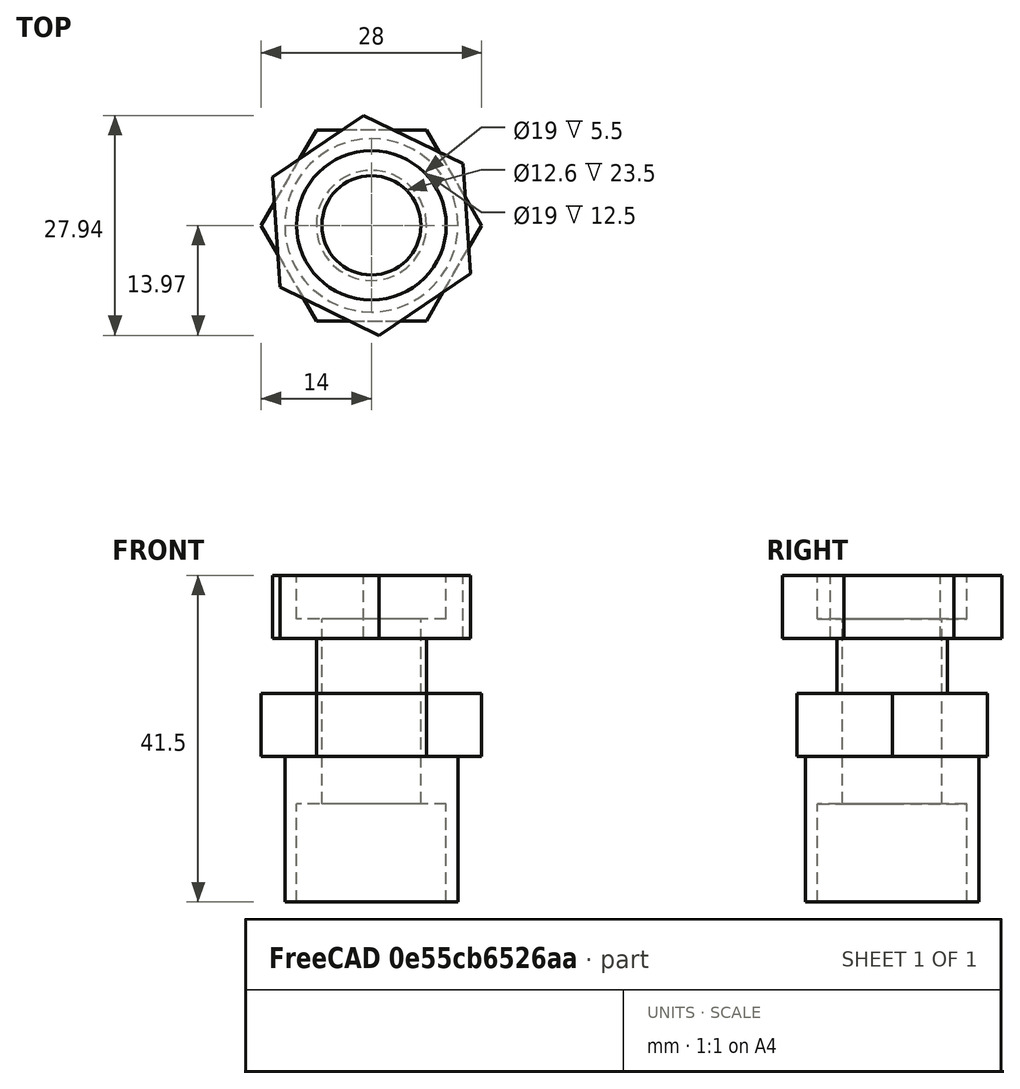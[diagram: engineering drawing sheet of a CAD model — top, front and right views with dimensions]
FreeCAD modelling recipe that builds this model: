
FCSTD DOCUMENT  (FreeCAD 0.16R6706 (Git))
Label: 1_2_ to 3_4_swivel
License: All rights reserved
LicenseURL: http://en.wikipedia.org/wiki/All_rights_reserved
objects: Part::Cylinder×10, Part::Part2DObjectPython×4, Part::FeaturePython×4, Part::Extrusion×4, Part::MultiFuse×4, Part::Cut×2, Part::Fuse×1
note: 29 computed .brp shape members not serialized (recipe doc carries the construction recipe); baked Part::Feature solids carry a one-line shape summary decoded from their .brp

FEATURE [Part::Cylinder] cylinder
  Angle = 360
  Height = 25
  Placement = pos=(0,0,-22.5) rot=(0,0,1;0rad)
  Radius = 11
FEATURE [Part::Cylinder] cylinder001
  Angle = 360
  Height = 30
  Placement = pos=(0,0,-15) rot=(0,0,1;0rad)
  Radius = 7
FEATURE [Part::Part2DObjectPython] polygon  # Draft 2D object (typed FeaturePython)
  ChamferSize = 0
  DrawMode = 0
  FacesNumber = 6
  FilletRadius = 0
  MakeFace = true
  Radius = 14
FEATURE [Part::FeaturePython] RefineLinearExtrude  # WARN: FeaturePython — macro-defined, semantics opaque (R4)
  Base = -> polygon
FEATURE [Part::Extrusion] LinearExtrude
  Base = -> RefineLinearExtrude
  Dir = (0,0,8)
  Placement = pos=(0,0,-4) rot=(0,0,1;0rad)
  Solid = true
FEATURE [Part::Part2DObjectPython] polygon001  # Draft 2D object (typed FeaturePython)
  ChamferSize = 0
  DrawMode = 0
  FacesNumber = 6
  FilletRadius = 0
  MakeFace = true
  Radius = 14
FEATURE [Part::FeaturePython] RefineLinearExtrude001  # WARN: FeaturePython — macro-defined, semantics opaque (R4)
  Base = -> polygon001
FEATURE [Part::Extrusion] LinearExtrude001
  Base = -> RefineLinearExtrude001
  Dir = (0,0,8)
  Placement = pos=(0,0,11) rot=(0,0,1;0.593412rad)
  Solid = true
FEATURE [Part::MultiFuse] Group
  Shapes = -> [cylinder,cylinder001,LinearExtrude,LinearExtrude001]
FEATURE [Part::Cylinder] cylinder002
  Angle = 360
  Height = 20
  Placement = pos=(0,0,-30) rot=(0,0,1;0rad)
  Radius = 9.5
FEATURE [Part::Cylinder] cylinder003
  Angle = 360
  Height = 50
  Placement = pos=(0,0,-15) rot=(0,0,1;0rad)
  Radius = 6.3
FEATURE [Part::Cylinder] cylinder004
  Angle = 360
  Height = 13
  Placement = pos=(0,0,13.5) rot=(0,0,1;0rad)
  Radius = 9.5
FEATURE [Part::MultiFuse] Group001
  Shapes = -> [cylinder002,cylinder003,cylinder004]
FEATURE [Part::Cut] difference
  Base = -> Group
  Tool = -> Group001
FEATURE [Part::Cylinder] cylinder005
  Angle = 360
  Height = 25
  Placement = pos=(0,0,-22.5) rot=(0,0,1;0rad)
  Radius = 11
FEATURE [Part::Cylinder] cylinder006
  Angle = 360
  Height = 30
  Placement = pos=(0,0,-15) rot=(0,0,1;0rad)
  Radius = 7
FEATURE [Part::Part2DObjectPython] polygon002  # Draft 2D object (typed FeaturePython)
  ChamferSize = 0
  DrawMode = 0
  FacesNumber = 6
  FilletRadius = 0
  MakeFace = true
  Radius = 14
FEATURE [Part::FeaturePython] RefineLinearExtrude002  # WARN: FeaturePython — macro-defined, semantics opaque (R4)
  Base = -> polygon002
FEATURE [Part::Extrusion] LinearExtrude002
  Base = -> RefineLinearExtrude002
  Dir = (0,0,8)
  Placement = pos=(0,0,-4) rot=(0,0,1;0rad)
  Solid = true
FEATURE [Part::Part2DObjectPython] polygon003  # Draft 2D object (typed FeaturePython)
  ChamferSize = 0
  DrawMode = 0
  FacesNumber = 6
  FilletRadius = 0
  MakeFace = true
  Radius = 14
FEATURE [Part::FeaturePython] RefineLinearExtrude003  # WARN: FeaturePython — macro-defined, semantics opaque (R4)
  Base = -> polygon003
FEATURE [Part::Extrusion] LinearExtrude003
  Base = -> RefineLinearExtrude003
  Dir = (0,0,8)
  Placement = pos=(0,0,11) rot=(0,0,1;0.593412rad)
  Solid = true
FEATURE [Part::MultiFuse] Group002
  Shapes = -> [cylinder005,cylinder006,LinearExtrude002,LinearExtrude003]
FEATURE [Part::Cylinder] cylinder007
  Angle = 360
  Height = 20
  Placement = pos=(0,0,-30) rot=(0,0,1;0rad)
  Radius = 9.5
FEATURE [Part::Cylinder] cylinder008
  Angle = 360
  Height = 50
  Placement = pos=(0,0,-15) rot=(0,0,1;0rad)
  Radius = 6.3
FEATURE [Part::Cylinder] cylinder009
  Angle = 360
  Height = 13
  Placement = pos=(0,0,13.5) rot=(0,0,1;0rad)
  Radius = 9.5
FEATURE [Part::MultiFuse] Group003
  Shapes = -> [cylinder007,cylinder008,cylinder009]
FEATURE [Part::Cut] difference001
  Base = -> Group002
  Tool = -> Group003
FEATURE [Part::Fuse] Group004
  Base = -> difference
  Tool = -> difference001
